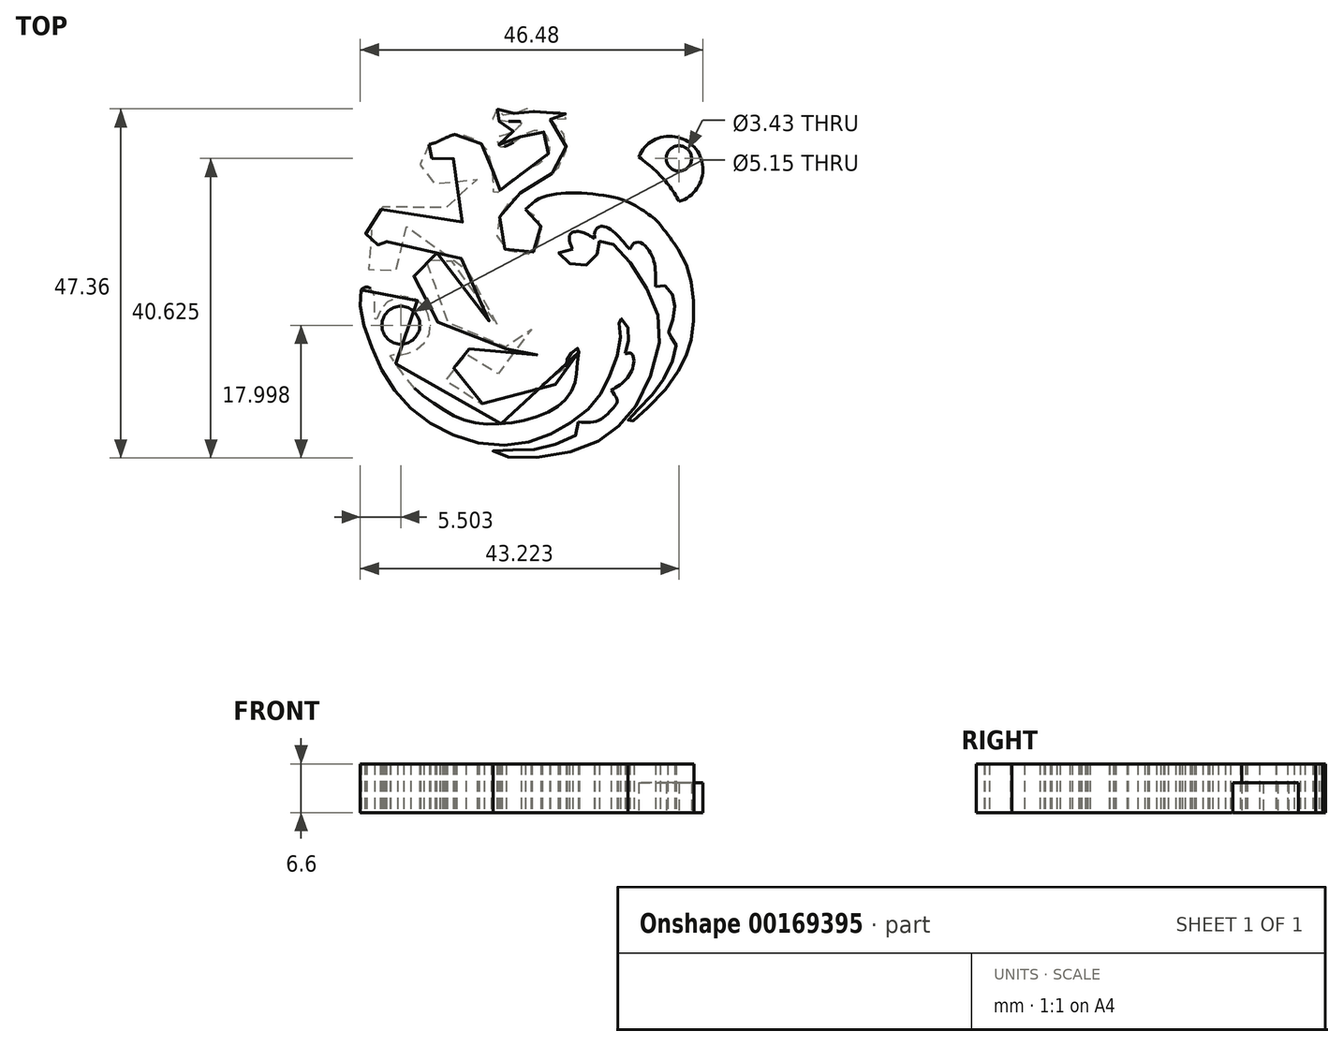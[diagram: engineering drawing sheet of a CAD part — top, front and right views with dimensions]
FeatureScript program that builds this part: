
annotation { "Feature Type Name" : "Feature", "Feature Type Description" : "" }
export const myFeature = defineFeature(function(context is Context, id is Id, definition is map)
    precondition{}
    {
        {
            var Q0;
            Q0=qCreatedBy(makeId("Top.planeOp"),FACE);
            var sketch = newSketch(context, id + "F0", { "sketchPlane" : qUnion([Q0])});
            skFitSpline(sketch, "E0", {"points": [v(-12.33, -10.91) * mm, v(-12.4, -13.83) * mm, v(-10.84, -18.96) * mm, v(-7.85, -24.5) * mm, v(-3.3, -28.78) * mm, v(3.18, -31.62) * mm, v(10.09, -31.62) * mm, v(15.28, -29.42) * mm, v(19.27, -26.29) * mm, v(21.4, -22.51) * mm, v(22.75, -18.24) * mm, v(22.68, -15.68) * mm, v(22.54, -14.9) * mm, v(23.04, -14.9) * mm, v(23.82, -15.97) * mm, v(23.9, -17.75) * mm, v(23.46, -19.6) * mm], "startDerivative": vector(-5.55, -48.27) * mm, "endDerivative": vector(-11.03, -40.25) * mm});
            skFitSpline(sketch, "E1", {"points": [v(23.46, -19.6) * mm, v(24.32, -19.6) * mm, v(24.6, -21.02) * mm, v(23.46, -23.23) * mm, v(21.54, -24.58) * mm], "startDerivative": vector(5.44, 1.34) * mm, "endDerivative": vector(-6.98, -3.94) * mm});
            skFitSpline(sketch, "E2", {"points": [v(21.54, -24.58) * mm, v(22.4, -26) * mm, v(21.54, -27.28) * mm, v(19.7, -28.7) * mm, v(17.13, -28.85) * mm], "startDerivative": vector(5.66, -6.4) * mm, "endDerivative": vector(-9.57, 0.77) * mm});
            skFitSpline(sketch, "E3", {"points": [v(17.13, -28.85) * mm, v(17.13, -30.27) * mm, v(14.85, -31.62) * mm, v(11.5, -32.55) * mm, v(8.6, -32.7) * mm, v(5.53, -32.76) * mm, v(6.38, -33.33) * mm, v(10.94, -33.69) * mm, v(18.34, -32.2) * mm, v(22.25, -29.7) * mm, v(25.39, -25.86) * mm, v(28.1, -18.32) * mm, v(27.52, -13.12) * mm, v(24.46, -7.64) * mm, v(21.54, -4.58) * mm, v(20.05, -4.23) * mm, v(19.98, -5.08) * mm, v(19.4, -6.43) * mm, v(18.27, -7.5) * mm, v(17.13, -7.71) * mm, v(14.43, -6.43) * mm, v(14.71, -5.65) * mm, v(16.35, -5.44) * mm], "startDerivative": vector(11, -47.62) * mm, "endDerivative": vector(54.6, -1.37) * mm});
            skFitSpline(sketch, "E4", {"points": [v(16.35, -5.44) * mm, v(15.94, -4.32) * mm, v(16, -3.4) * mm, v(16.64, -3.05) * mm, v(17.57, -3.11) * mm, v(19.32, -3.96) * mm], "startDerivative": vector(-2.37, 5.32) * mm, "endDerivative": vector(7.07, -3.92) * mm});
            skFitSpline(sketch, "E5", {"points": [v(19.32, -3.96) * mm, v(19.32, -3.17) * mm, v(19.75, -2.48) * mm, v(20.47, -2.33) * mm, v(21.65, -2.88) * mm, v(23.15, -4.34) * mm, v(24.08, -5.44) * mm], "startDerivative": vector(-0.65, 5.66) * mm, "endDerivative": vector(4.6, -5.56) * mm});
            skFitSpline(sketch, "E6", {"points": [v(24.08, -5.44) * mm, v(24.42, -4.87) * mm, v(25.12, -4.46) * mm, v(26.28, -5.1) * mm, v(27.22, -6.58) * mm, v(27.53, -8.2) * mm, v(27.6, -10.52) * mm], "startDerivative": vector(2.39, 4.97) * mm, "endDerivative": vector(0.07, -11.1) * mm});
            skFitSpline(sketch, "E7", {"points": [v(27.6, -10.52) * mm, v(28.3, -10.34) * mm, v(29.32, -10.63) * mm, v(30, -11.94) * mm, v(30.17, -13.22) * mm, v(29.93, -14.9) * mm, v(29.42, -16.61) * mm, v(29.23, -17.06) * mm, v(29.6, -17.29) * mm, v(30.21, -17.82) * mm, v(30.26, -19.25) * mm, v(28.94, -22.61) * mm, v(26.82, -25.51) * mm, v(24.33, -28.06) * mm, v(23.87, -28.76) * mm, v(24.08, -28.94) * mm, v(25.34, -28.03) * mm, v(29.33, -23.97) * mm, v(31.32, -20.68) * mm, v(32.23, -18.35) * mm, v(32.76, -14.92) * mm, v(32.64, -11.26) * mm, v(32, -8.11) * mm, v(30.65, -5.44) * mm, v(28.2, -2.1) * mm, v(27.04, -1) * mm, v(24.08, 0.89) * mm, v(21.8, 1.62) * mm, v(18, 2.2) * mm, v(14.46, 2.1) * mm, v(11.83, 1.46) * mm, v(9.93, 0) * mm], "startDerivative": vector(35.02, 12.33) * mm, "endDerivative": vector(-52.33, -48.88) * mm});
            skFitSpline(sketch, "E8", {"points": [v(9.93, 0) * mm, v(10.93, -0.63) * mm, v(11.84, -1.52) * mm, v(12.05, -2.58) * mm, v(11.93, -3.96) * mm, v(11.15, -5.6) * mm, v(10.59, -6.1) * mm, v(8.8, -5.98) * mm, v(6.58, -4.9) * mm, v(6.13, -2.34) * mm, v(6.71, -0.47) * mm, v(8.09, 1.33) * mm, v(9.67, 2.5) * mm, v(12.53, 4.12) * mm, v(14.03, 5.32) * mm, v(15.22, 6.94) * mm, v(15.45, 8.97) * mm, v(14.9, 10.54) * mm, v(13.3, 12.26) * mm, v(13.67, 12.3) * mm, v(15.91, 12.43) * mm, v(14.77, 13.16) * mm, v(12.3, 13.1) * mm, v(11.02, 13.26) * mm, v(9.93, 13.6) * mm, v(9.15, 13.07) * mm, v(8.45, 13.04) * mm, v(7.82, 12.8) * mm, v(6.41, 12.96) * mm, v(6.32, 13.52) * mm, v(5.98, 13.46) * mm, v(5.77, 12.83) * mm, v(5.45, 12.25) * mm, v(5.42, 12) * mm, v(9.03, 11.92) * mm, v(9.37, 11.66) * mm, v(7.86, 10.35) * mm, v(6.1, 9.7) * mm, v(6.11, 9.33) * mm, v(6.34, 8.69) * mm, v(6.82, 8.48) * mm, v(8.55, 9.22) * mm, v(9.4, 9.93) * mm, v(10.57, 10.53) * mm, v(12, 10.78) * mm, v(12.8, 9.94) * mm, v(13.08, 9.27) * mm, v(13.23, 8.24) * mm, v(12.57, 6.76) * mm, v(10.97, 5.75) * mm, v(8.97, 4.57) * mm, v(7.74, 3.63) * mm, v(6.37, 2.46) * mm, v(5.74, 2.09) * mm, v(5.57, 4.3) * mm, v(5.2, 6.71) * mm, v(4.59, 8.2) * mm, v(3.4, 9.25) * mm, v(1.53, 10.03) * mm, v(0.35, 10.14) * mm, v(-1.64, 9.34) * mm, v(-3.12, 8.8) * mm], "startDerivative": vector(65.75, -39.44) * mm, "endDerivative": vector(-80.06, -27.02) * mm});
            skFitSpline(sketch, "E9", {"points": [v(0.35, 10.14) * mm, v(1.01, 10.7) * mm, v(1.79, 11.5) * mm, v(1.92, 11.98) * mm, v(1.28, 11.59) * mm, v(0.35, 11) * mm, v(-0.35, 10.6) * mm, v(-1.64, 9.34) * mm, v(-3.12, 8.8) * mm, v(-3.94, 8.36) * mm, v(-4.47, 7.56) * mm, v(-5.06, 6.8) * mm, v(-5.98, 5.93) * mm, v(-6.57, 5.3) * mm, v(-6.43, 4.68) * mm, v(-5.75, 4.9) * mm, v(-4.61, 5.84) * mm, v(-3.54, 6.64) * mm, v(-2.88, 6.92) * mm, v(-2.36, 6.7) * mm, v(-2.65, 5.8) * mm, v(-3.34, 4.54) * mm, v(-3.85, 3.63) * mm, v(-3.4, 2.76) * mm, v(-2.54, 3.05) * mm, v(-2.3, 4.35) * mm, v(-1.49, 5.93) * mm, v(-0.44, 6.76) * mm, v(0.77, 6.85) * mm, v(2.12, 6.76) * mm, v(2.82, 5.84) * mm, v(3.33, 4.4) * mm, v(3.27, 3) * mm, v(2.99, 1.33) * mm, v(2.7, -0.59) * mm, v(2.15, -2.16) * mm, v(1.1, -1.46) * mm, v(0.35, -0.51) * mm, v(-1.43, 0.47) * mm, v(-3.61, 0.74) * mm, v(-6.43, 0.46) * mm, v(-8.64, -0.59) * mm, v(-9.75, -0.89) * mm, v(-9.54, -0.53) * mm, v(-9.6, 0) * mm, v(-9.34, 0.46) * mm, v(-9.06, 1.39) * mm, v(-9.01, 2.96) * mm, v(-9.27, 2.94) * mm, v(-9.24, 2.2) * mm, v(-9.72, 1.13) * mm, v(-10.21, 0.43) * mm, v(-10.39, -0.48) * mm, v(-10.87, -1.95) * mm, v(-11.62, -3.07) * mm, v(-11.84, -3.9) * mm, v(-11.62, -4.4) * mm, v(-11.81, -5.05) * mm, v(-11.83, -5.95) * mm, v(-12.13, -6.83) * mm, v(-12.33, -7.55) * mm, v(-12.08, -8.1) * mm, v(-11.33, -8.16) * mm, v(-10.88, -6.65) * mm, v(-10.45, -5.05) * mm, v(-10.15, -4.78) * mm, v(-9.72, -5.6) * mm, v(-9.5, -6.93) * mm, v(-9, -8.02) * mm, v(-7.95, -8.37) * mm, v(-7.7, -8.37) * mm, v(-7.4, -7.98) * mm, v(-8.18, -7.85) * mm, v(-8.34, -6.81) * mm, v(-8.68, -5.59) * mm, v(-8.73, -5.32) * mm, v(-8.95, -4.54) * mm, v(-7.56, -3.64) * mm, v(-6.7, -2.86) * mm, v(-5.78, -2.09) * mm, v(-4.05, -1.74) * mm, v(-2.65, -1.85) * mm, v(-1.08, -2.82) * mm, v(0, -4.25) * mm, v(1.5, -7.23) * mm, v(2.61, -9.34) * mm, v(3.67, -10.8) * mm, v(4.86, -11.88) * mm, v(6.2, -12.48) * mm, v(6.11, -13.05) * mm, v(6.49, -15.28) * mm, v(6.44, -15.74) * mm, v(5.29, -15.28) * mm, v(3.45, -14.26) * mm, v(2.04, -12.96) * mm, v(0.9, -11.5) * mm, v(0.35, -9.66) * mm, v(0, -7.44) * mm, v(-0.2, -6.38) * mm, v(-1.22, -5.87) * mm, v(-2, -5.93) * mm, v(-2.18, -6.02) * mm, v(-1.32, -6.53) * mm, v(-2.15, -6.68) * mm, v(-3.27, -6.23) * mm, v(-4.32, -6.75) * mm, v(-3.5, -6.92) * mm, v(-3.12, -7.43) * mm, v(-4.06, -7.85) * mm, v(-5.4, -8.3) * mm, v(-5.56, -9.3) * mm, v(-5.17, -9.06) * mm, v(-4.61, -8.77) * mm, v(-4.24, -8.97) * mm, v(-3.27, -9.64) * mm, v(-1.64, -11.1) * mm, v(-1.2, -12.48) * mm, v(-1.64, -13.62) * mm, v(-1.64, -13.96) * mm, v(-1.13, -14.56) * mm, v(-1.92, -15.06) * mm, v(-2.15, -14.9) * mm, v(-1.94, -15.37) * mm, v(-0.92, -15.6) * mm, v(-0.23, -14.82) * mm, v(0.2, -14.6) * mm, v(0.13, -13.81) * mm, v(0.35, -13.34) * mm, v(0.94, -14.08) * mm, v(3.91, -16.75) * mm, v(7.11, -18.5) * mm, v(7.32, -18.89) * mm, v(6.73, -19.7) * mm, v(7.19, -19.87) * mm, v(8.06, -19.48) * mm, v(8.5, -18.72) * mm, v(9.57, -16.48) * mm, v(10.78, -15.07) * mm, v(10.73, -16.2) * mm, v(10.97, -18.6) * mm, v(11.89, -20.3) * mm, v(12.2, -20.8) * mm, v(11.12, -21.94) * mm, v(8.8, -22.36) * mm, v(6.32, -22.34) * mm, v(4.47, -21.6) * mm, v(3.06, -19.74) * mm, v(2.52, -18.93) * mm, v(2.18, -19) * mm, v(1.16, -18.68) * mm, v(0.47, -19.04) * mm, v(1, -19.17) * mm, v(1.85, -19.68) * mm, v(1.55, -19.9) * mm, v(0.65, -20.04) * mm, v(-0.58, -20.41) * mm, v(-0.62, -21.04) * mm, v(-0.32, -20.83) * mm, v(0.53, -20.9) * mm, v(0.55, -21.3) * mm, v(-0.3, -21.83) * mm, v(-0.87, -22.64) * mm, v(-0.74, -23.72) * mm, v(-0.49, -23.2) * mm, v(0.13, -22.93) * mm, v(1.62, -22.87) * mm, v(2.76, -23.1) * mm, v(3.99, -24.08) * mm, v(4.17, -24.92) * mm, v(4.29, -26) * mm, v(3.64, -27.1) * mm, v(4.7, -27.11) * mm, v(5.48, -26) * mm, v(5.33, -24.26) * mm, v(5.93, -23.76) * mm, v(8.33, -24.21) * mm, v(12.49, -24.29) * mm, v(14.13, -23.69) * mm, v(14.6, -23.58) * mm, v(14.49, -24.4) * mm, v(14.46, -25.14) * mm, v(15.31, -24.33) * mm, v(15.57, -23.02) * mm, v(15.5, -21.62) * mm, v(15.57, -20.35) * mm, v(16.45, -19.25) * mm, v(17.1, -18.86) * mm, v(17.1, -19.77) * mm, v(16.84, -22.39) * mm, v(16.45, -24.08) * mm, v(15.22, -26) * mm, v(13.4, -27.32) * mm, v(10.15, -28.58) * mm, v(6.8, -29.09) * mm, v(3.61, -29.06) * mm, v(0.86, -28.31) * mm, v(-1.44, -27.02) * mm, v(-4.44, -24.92) * mm, v(-6.08, -23.16) * mm, v(-7.86, -20.67) * mm, v(-8.4, -19.77) * mm, v(-8.2, -19.68) * mm, v(-7.5, -19.76) * mm, v(-6.14, -19.57) * mm, v(-4.39, -18.73) * mm, v(-3.12, -16.93) * mm, v(-3.12, -14.75) * mm, v(-4.24, -12.74) * mm, v(-6.48, -11.83) * mm, v(-8.26, -12.31) * mm, v(-9.55, -13.4) * mm, v(-10.42, -15.15) * mm, v(-10.52, -13.37) * mm, v(-10.78, -11.05) * mm, v(-11.69, -10.56) * mm, v(-12.33, -10.91) * mm], "startDerivative": vector(160.87, 135.14) * mm, "endDerivative": vector(-162.05, -138.92) * mm});
            skCircle(sketch, "E10", {"center": v(-6.97, -15.74) * mm, "radius": 2.57 * mm});
            skFitSpline(sketch, "E11", {"points": [v(16.13, 10.97) * mm, v(19.45, 10.46) * mm, v(23.45, 8.4) * mm, v(28.68, 4.09) * mm, v(31.56, -0.41) * mm, v(33.12, -3.93) * mm, v(33.97, -7.23) * mm, v(34.04, -12.9) * mm], "startDerivative": vector(27.34, -2.1) * mm, "endDerivative": vector(-1.26, -38.5) * mm});
            skFitSpline(sketch, "E12", {"points": [v(34.04, -12.9) * mm, v(33.15, -9.83) * mm, v(31.21, -4.15) * mm, v(27.63, 1.52) * mm, v(24.53, 5.07) * mm, v(23.16, 6.43) * mm, v(23.04, 5.86) * mm, v(22.66, 3.52) * mm, v(19.83, 2.6) * mm, v(17.36, 3.83) * mm, v(16.6, 6.34) * mm, v(17.55, 8.2) * mm, v(19.33, 8.78) * mm, v(17.46, 9.48) * mm, v(16.13, 10.97) * mm], "startDerivative": vector(-10.8, 36.95) * mm, "endDerivative": vector(-14.95, 27.64) * mm});
            skCircle(sketch, "E13", {"center": v(20.18, 5.83) * mm, "radius": 1.64 * mm});
            skLineSegment(sketch, "E14", {"start": v(25.45, 4.03) * mm, "end": v(24.08, 0.89) * mm});
            skLineSegment(sketch, "E15", {"start": v(31.21, -4.15) * mm, "end": v(30.65, -5.44) * mm});
            skCircle(sketch, "E16", {"center": v(30.75, 6.88) * mm, "radius": 1.71 * mm});
            skArc(sketch, "E17", {"start": v(30.8, 1.06) * mm, "mid": v(32.83, 8.43) * mm, "end": v(25.3, 7.1) * mm});
            skSolve(sketch);
        }
        {
            var Q0;
            Q0=makeQuery(id+"F0.imprint","IMPRINT",FACE,{"disambiguationData":[TD([[makeQuery(id+"F0.imprint","IMPRINT",EDGE,{"derivedFrom":sQuery(id+"F0.wireOp",EDGE,"E0")}),1.0]])]});
            extrude(context, id + "F1", {"entities" : qUnion([Q0]), "depth" : 6.6 * mm});
        }
        {
            var Q0;
            Q0=makeQuery(id+"F0.imprint","IMPRINT",FACE,{"disambiguationData":[TD([[makeQuery(id+"F0.imprint","IMPRINT",EDGE,{"derivedFrom":sQuery(id+"F0.wireOp",EDGE,"E16")}),-1.0]])]});
            extrude(context, id + "F2", {"entities" : qUnion([Q0]), "operationType" : NewBodyOperationType.ADD, "depth" : 4.06 * mm});
        }
    });
